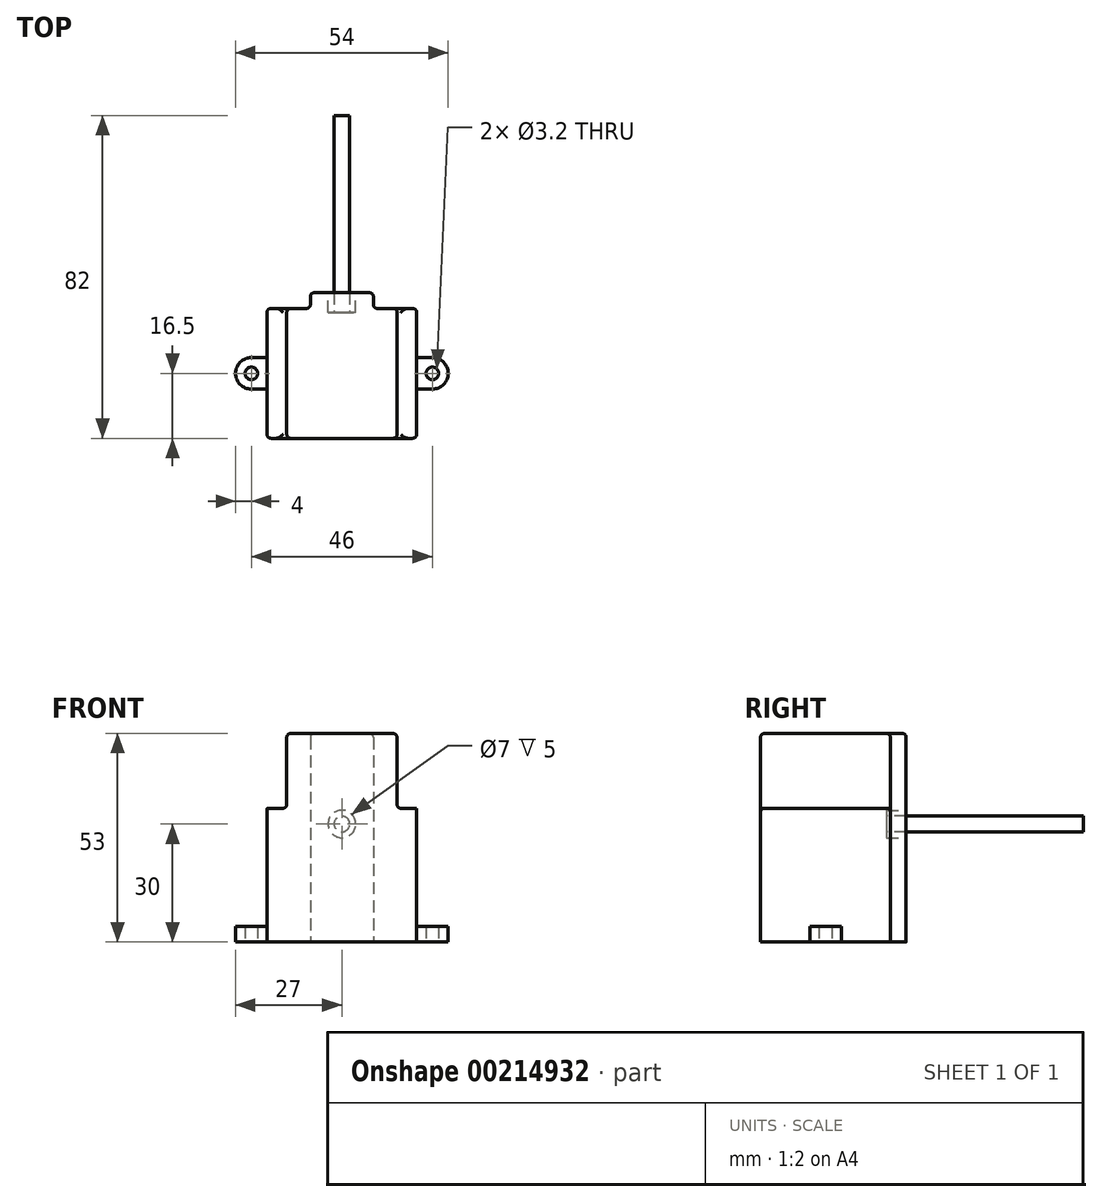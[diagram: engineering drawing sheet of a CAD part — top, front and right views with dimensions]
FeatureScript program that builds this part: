
annotation { "Feature Type Name" : "Feature", "Feature Type Description" : "" }
export const myFeature = defineFeature(function(context is Context, id is Id, definition is map)
    precondition{}
    {
        {
            var Q0;
            Q0=qCreatedBy(makeId("Top.planeOp"),FACE);
            var sketch = newSketch(context, id + "F0", { "sketchPlane" : qUnion([Q0])});
            skLineSegment(sketch, "E0.bottom", {"start": v(19, 16.5) * mm, "end": v(8, 16.5) * mm});
            skLineSegment(sketch, "E0.top", {"start": v(19, -16.5) * mm, "end": v(-19, -16.5) * mm});
            skLineSegment(sketch, "E0.left", {"start": v(19, 16.5) * mm, "end": v(19, -16.5) * mm});
            skLineSegment(sketch, "E0.right", {"start": v(-19, 16.5) * mm, "end": v(-19, -16.5) * mm});
            skPoint(sketch, "E0.middle", {"position": v(0, 0) * mm});
            skLineSegment(sketch, "E1", {"start": v(0, 16.5) * mm, "end": v(0, 30.54) * mm, "construction": true});
            skLineSegment(sketch, "E2", {"start": v(-8, 16.5) * mm, "end": v(-8, 20.5) * mm});
            skLineSegment(sketch, "E3", {"start": v(-8, 20.5) * mm, "end": v(0, 20.5) * mm});
            skLineSegment(sketch, "E4.MirrorCS", {"start": v(8, 20.5) * mm, "end": v(0, 20.5) * mm});
            skLineSegment(sketch, "E5.MirrorCS", {"start": v(8, 16.5) * mm, "end": v(8, 20.5) * mm});
            skLineSegment(sketch, "E6.trimOffspring", {"start": v(-8, 16.5) * mm, "end": v(-19, 16.5) * mm});
            skCircle(sketch, "E7", {"center": v(-23, 0) * mm, "radius": 1.6 * mm});
            skPoint(sketch, "E7.centerSnap0", {"position": v(-19, 0) * mm});
            skCircle(sketch, "E8", {"center": v(23, 0) * mm, "radius": 1.6 * mm});
            skArc(sketch, "E9", {"start": v(-23, 4) * mm, "mid": v(-27, 0) * mm, "end": v(-23, -4) * mm});
            skLineSegment(sketch, "E10", {"start": v(-23, 4) * mm, "end": v(-19, 4) * mm});
            skLineSegment(sketch, "E11", {"start": v(-23, -4) * mm, "end": v(-19, -4) * mm});
            skLineSegment(sketch, "E12.MirrorCS", {"start": v(23, 4) * mm, "end": v(19, 4) * mm});
            skArc(sketch, "E13.MirrorCS", {"start": v(23, 4) * mm, "mid": v(27, 0) * mm, "end": v(23, -4) * mm});
            skLineSegment(sketch, "E14.MirrorCS", {"start": v(23, -4) * mm, "end": v(19, -4) * mm});
            skSolve(sketch);
        }
        {
            var Q0;
            {var subQ7=sQuery(id+"F0.wireOp",EDGE,"E0.bottom");Q0=makeQuery(id+"F0.imprint","IMPRINT",FACE,{"disambiguationData":[TD([[makeQuery(id+"F0.imprint","IMPRINT",EDGE,{"derivedFrom":subQ7}),1.0]])]});}
            extrude(context, id + "F1", {"entities" : qUnion([Q0]), "depth" : 53 * mm, "offsetDistance" : 25 * mm});
        }
        {
            var Q0;
            Q0=makeQuery(id+"F1.opExtrude","CAP_FACE",FACE,{"disambiguationData":[OSD([sQuery(id+"F0.wireOp",EDGE,"E0.bottom"),sQuery(id+"F0.wireOp",EDGE,"E0.top"),sQuery(id+"F0.wireOp",EDGE,"E0.left"),sQuery(id+"F0.wireOp",EDGE,"E0.right"),sQuery(id+"F0.wireOp",EDGE,"E2"),sQuery(id+"F0.wireOp",EDGE,"E3"),sQuery(id+"F0.wireOp",EDGE,"E4.MirrorCS"),sQuery(id+"F0.wireOp",EDGE,"E5.MirrorCS"),sQuery(id+"F0.wireOp",EDGE,"E6.trimOffspring")])],"isStart":false});
            var sketch = newSketch(context, id + "F2", { "sketchPlane" : qUnion([Q0])});
            skLineSegment(sketch, "E15.0", {"start": v(-19, 16.5) * mm, "end": v(-19, -16.5) * mm});
            skLineSegment(sketch, "E15.1", {"start": v(19, 16.5) * mm, "end": v(19, -16.5) * mm});
            skLineSegment(sketch, "E16.0", {"start": v(-14, 16.5) * mm, "end": v(-14, -16.5) * mm});
            skLineSegment(sketch, "E17.0", {"start": v(14, 16.5) * mm, "end": v(14, -16.5) * mm});
            skLineSegment(sketch, "E18", {"start": v(-19, 16.5) * mm, "end": v(-14, 16.5) * mm});
            skLineSegment(sketch, "E19", {"start": v(-19, -16.5) * mm, "end": v(-14, -16.5) * mm});
            skLineSegment(sketch, "E20", {"start": v(14, -16.5) * mm, "end": v(19, -16.5) * mm});
            skLineSegment(sketch, "E21", {"start": v(19, 16.5) * mm, "end": v(14, 16.5) * mm});
            skSolve(sketch);
        }
        {
            var Q0;
            Q0 = qSketchRegion(id + "F2", true);
            extrude(context, id + "F3", {"entities" : qUnion([Q0]), "operationType" : NewBodyOperationType.REMOVE, "oppositeDirection" : true, "depth" : 19 * mm, "offsetDistance" : 25 * mm});
        }
        {
            var Q0;
            Q0=makeQuery(id+"F1.opExtrude","SWEPT_FACE",FACE,{"disambiguationData":[OSD([sQuery(id+"F0.wireOp",EDGE,"E3"),sQuery(id+"F0.wireOp",EDGE,"E4.MirrorCS")])]});
            var sketch = newSketch(context, id + "F4", { "sketchPlane" : qUnion([Q0])});
            skCircle(sketch, "E22", {"center": v(0, 30) * mm, "radius": 3.5 * mm});
            skPoint(sketch, "E22.centerSnap0", {"position": v(0, 53) * mm});
            skSolve(sketch);
        }
        {
            var Q0;
            Q0=makeQuery(id+"F4.imprint","IMPRINT",FACE,{"disambiguationData":[TD([[makeQuery(id+"F4.imprint","IMPRINT",EDGE,{"derivedFrom":sQuery(id+"F4.wireOp",EDGE,"E22")}),1.0]])]});
            extrude(context, id + "F5", {"entities" : qUnion([Q0]), "operationType" : NewBodyOperationType.REMOVE, "oppositeDirection" : true, "depth" : 5 * mm, "offsetDistance" : 25 * mm});
        }
        {
            var Q0;
            Q0=makeQuery(id+"F0.imprint","IMPRINT",FACE,{"disambiguationData":[TD([[makeQuery(id+"F0.imprint","IMPRINT",EDGE,{"derivedFrom":sQuery(id+"F0.wireOp",EDGE,"E7")}),-1.0]])]});
            var Q1;
            Q1=makeQuery(id+"F0.imprint","IMPRINT",FACE,{"disambiguationData":[TD([[makeQuery(id+"F0.imprint","IMPRINT",EDGE,{"derivedFrom":sQuery(id+"F0.wireOp",EDGE,"E8")}),-1.0]])]});
            extrude(context, id + "F6", {"entities" : qUnion([Q0, Q1]), "operationType" : NewBodyOperationType.ADD, "depth" : 4 * mm, "offsetDistance" : 25 * mm});
        }
        {
            var Q0;
            Q0=makeQuery(id+"F5.boolean.opBoolean","COPY",FACE,{"derivedFrom":makeQuery(id+"F5.opExtrude","CAP_FACE",FACE,{"disambiguationData":[OSD([sQuery(id+"F4.wireOp",EDGE,"E22")])],"isStart":false})});
            var sketch = newSketch(context, id + "F7", { "sketchPlane" : qUnion([Q0])});
            skCircle(sketch, "E23", {"center": v(0, 30) * mm, "radius": 2 * mm});
            skSolve(sketch);
        }
        {
            var Q0;
            Q0 = qSketchRegion(id + "F7", true);
            extrude(context, id + "F8", {"entities" : qUnion([Q0]), "operationType" : NewBodyOperationType.ADD, "depth" : 50 * mm, "offsetDistance" : 25 * mm});
        }
        {
            var Q0;
            Q0=makeQuery(id+"F1.opExtrude","CAP_FACE",FACE,{"disambiguationData":[OSD([sQuery(id+"F0.wireOp",EDGE,"E0.bottom"),sQuery(id+"F0.wireOp",EDGE,"E0.top"),sQuery(id+"F0.wireOp",EDGE,"E0.left"),sQuery(id+"F0.wireOp",EDGE,"E0.right"),sQuery(id+"F0.wireOp",EDGE,"E2"),sQuery(id+"F0.wireOp",EDGE,"E3"),sQuery(id+"F0.wireOp",EDGE,"E4.MirrorCS"),sQuery(id+"F0.wireOp",EDGE,"E5.MirrorCS"),sQuery(id+"F0.wireOp",EDGE,"E6.trimOffspring")])],"isStart":false});
            var Q1;
            Q1=makeQuery(id+"F3.boolean.opBoolean","COPY",FACE,{"derivedFrom":makeQuery(id+"F3.opExtrude","SWEPT_FACE",FACE,{"disambiguationData":[OSD([sQuery(id+"F2.wireOp",EDGE,"E16.0")])]})});
            var Q2;
            Q2=makeQuery(id+"F3.boolean.opBoolean","COPY",FACE,{"derivedFrom":makeQuery(id+"F3.opExtrude","SWEPT_FACE",FACE,{"disambiguationData":[OSD([sQuery(id+"F2.wireOp",EDGE,"E17.0")])]})});
            var Q3;
            Q3=makeQuery(id+"F1.opExtrude","SWEPT_EDGE",EDGE,{"disambiguationData":[OSD([sQuery(id+"F0.wireOp",EDGE,"E0.top"),sQuery(id+"F0.wireOp",EDGE,"E0.right")])]});
            var Q4;
            Q4=makeQuery(id+"F3.boolean.opBoolean","COPY",EDGE,{"derivedFrom":makeQuery(id+"F3.opExtrude","CAP_EDGE",EDGE,{"disambiguationData":[OSD([sQuery(id+"F2.wireOp",EDGE,"E19")])],"isStart":false})});
            var Q5;
            Q5=makeQuery(id+"F3.boolean.opBoolean","COPY",EDGE,{"derivedFrom":makeQuery(id+"F3.opExtrude","CAP_EDGE",EDGE,{"disambiguationData":[OSD([sQuery(id+"F2.wireOp",EDGE,"E20")])],"isStart":false})});
            var Q6;
            Q6=makeQuery(id+"F1.opExtrude","SWEPT_EDGE",EDGE,{"disambiguationData":[OSD([sQuery(id+"F0.wireOp",EDGE,"E0.top"),sQuery(id+"F0.wireOp",EDGE,"E0.left")])]});
            var Q7;
            Q7=makeQuery(id+"F3.boolean.opBoolean","COPY",EDGE,{"derivedFrom":makeQuery(id+"F3.opExtrude","CAP_EDGE",EDGE,{"disambiguationData":[OSD([sQuery(id+"F2.wireOp",EDGE,"E15.1")])],"isStart":false})});
            var Q8;
            Q8=makeQuery(id+"F1.opExtrude","SWEPT_EDGE",EDGE,{"disambiguationData":[OSD([sQuery(id+"F0.wireOp",EDGE,"E0.bottom"),sQuery(id+"F0.wireOp",EDGE,"E0.left")])]});
            var Q9;
            Q9=makeQuery(id+"F6.opExtrude","CAP_EDGE",EDGE,{"disambiguationData":[OSD([sQuery(id+"F0.wireOp",EDGE,"E0.left")])],"isStart":false});
            var Q10;
            Q10=makeQuery(id+"F6.opExtrude","SWEPT_EDGE",EDGE,{"disambiguationData":[OSD([sQuery(id+"F0.wireOp",EDGE,"E0.left"),sQuery(id+"F0.wireOp",EDGE,"E14.MirrorCS")])]});
            var Q11;
            Q11=makeQuery(id+"F6.opExtrude","SWEPT_EDGE",EDGE,{"disambiguationData":[OSD([sQuery(id+"F0.wireOp",EDGE,"E0.left"),sQuery(id+"F0.wireOp",EDGE,"E12.MirrorCS")])]});
            var Q12;
            Q12=makeQuery(id+"F1.opExtrude","SWEPT_EDGE",EDGE,{"disambiguationData":[OSD([sQuery(id+"F0.wireOp",EDGE,"E0.bottom"),sQuery(id+"F0.wireOp",EDGE,"E5.MirrorCS")])]});
            var Q13;
            Q13=makeQuery(id+"F1.opExtrude","SWEPT_EDGE",EDGE,{"disambiguationData":[OSD([sQuery(id+"F0.wireOp",EDGE,"E4.MirrorCS"),sQuery(id+"F0.wireOp",EDGE,"E5.MirrorCS")])]});
            var Q14;
            Q14=makeQuery(id+"F1.opExtrude","SWEPT_EDGE",EDGE,{"disambiguationData":[OSD([sQuery(id+"F0.wireOp",EDGE,"E2"),sQuery(id+"F0.wireOp",EDGE,"E3")])]});
            var Q15;
            Q15=makeQuery(id+"F1.opExtrude","SWEPT_EDGE",EDGE,{"disambiguationData":[OSD([sQuery(id+"F0.wireOp",EDGE,"E0.right"),sQuery(id+"F0.wireOp",EDGE,"E6.trimOffspring")])]});
            var Q16;
            Q16=makeQuery(id+"F1.opExtrude","SWEPT_EDGE",EDGE,{"disambiguationData":[OSD([sQuery(id+"F0.wireOp",EDGE,"E2"),sQuery(id+"F0.wireOp",EDGE,"E6.trimOffspring")])]});
            var Q17;
            Q17=makeQuery(id+"F3.boolean.opBoolean","COPY",EDGE,{"derivedFrom":makeQuery(id+"F3.opExtrude","CAP_EDGE",EDGE,{"disambiguationData":[OSD([sQuery(id+"F2.wireOp",EDGE,"E15.0")])],"isStart":false})});
            var Q18;
            Q18=makeQuery(id+"F6.opExtrude","SWEPT_EDGE",EDGE,{"disambiguationData":[OSD([sQuery(id+"F0.wireOp",EDGE,"E0.right"),sQuery(id+"F0.wireOp",EDGE,"E10")])]});
            var Q19;
            Q19=makeQuery(id+"F6.opExtrude","CAP_EDGE",EDGE,{"disambiguationData":[OSD([sQuery(id+"F0.wireOp",EDGE,"E0.right")])],"isStart":false});
            var Q20;
            Q20=makeQuery(id+"F6.opExtrude","SWEPT_EDGE",EDGE,{"disambiguationData":[OSD([sQuery(id+"F0.wireOp",EDGE,"E0.right"),sQuery(id+"F0.wireOp",EDGE,"E11")])]});
            var Q21;
            Q21=makeQuery(id+"F3.boolean.opBoolean","COPY",EDGE,{"derivedFrom":makeQuery(id+"F3.opExtrude","CAP_EDGE",EDGE,{"disambiguationData":[OSD([sQuery(id+"F2.wireOp",EDGE,"E21")])],"isStart":false})});
            var Q22;
            Q22=makeQuery(id+"F3.boolean.opBoolean","COPY",EDGE,{"derivedFrom":makeQuery(id+"F3.opExtrude","CAP_EDGE",EDGE,{"disambiguationData":[OSD([sQuery(id+"F2.wireOp",EDGE,"E18")])],"isStart":false})});
            fillet(context, id + "F9", {"entities" : qUnion([Q0, Q1, Q2, Q3, Q4, Q5, Q6, Q7, Q8, Q9, Q10, Q11, Q12, Q13, Q14, Q15, Q16, Q17, Q18, Q19, Q20, Q21, Q22]), "radius" : 1 * mm, "allowEdgeOverflow" : false});
        }
    });
